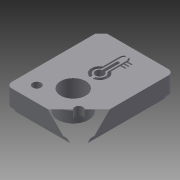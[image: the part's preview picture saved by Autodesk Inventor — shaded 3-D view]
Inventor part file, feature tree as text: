
AUTODESK INVENTOR PART (.ipt)
format: ipt  version: 2015 SP1 (Build 190203100, 203)  size: 237,056 bytes
history: native  units: mm
features: sketch x7, extrude x5, reference x4, other x2
ambient origin geometry x8: Origin, YZ Plane, XZ Plane, XY Plane, X Axis, Y Axis, Z Axis, Center Point
bodies: Body1 (feature_tree)
feature tree (18):
  other  "Sólido1"
  sketch  "Boceto1"  dims[d0=3.0mm d1=0.0mm]
  extrude  "Extrusión1"  Depth=1.0mm
  sketch  "Boceto3"  dims[d9=9.0mm d10=3.0mm d11=0.0mm]
  other  "Labio1"
  extrude  "Extrusión2"  Depth=3.0mm TaperAngle=0.0deg
  sketch  "Boceto7"
  extrude  "Extrusión3"  Depth=4.0mm TaperAngle=0.0deg
  extrude  "Extrusión4"  Depth=0.618mm
  extrude  "Extrusión5"  Depth=10.0mm TaperAngle=0.0deg
  sketch  "Boceto2"  dims[d2=1.0mm d3=1.0mm d4=0.0mm d5=0.0mm d6=0.0mm d7=0.0mm d8=9.5mm]
  reference  "Referencia1"
  reference  "Referencia2"
  sketch  "Boceto4"  dims[d12=11.0mm d13=4.0mm d14=0.0mm]
  reference  "Referencia3"
  reference  "Referencia4"
  sketch  "Boceto5"  dims[d16=10.0mm d17=0.0mm d31=0.618mm]
  sketch  "Boceto6"  dims[d35=1.0mm d36=10.0mm d37=0.0mm]
